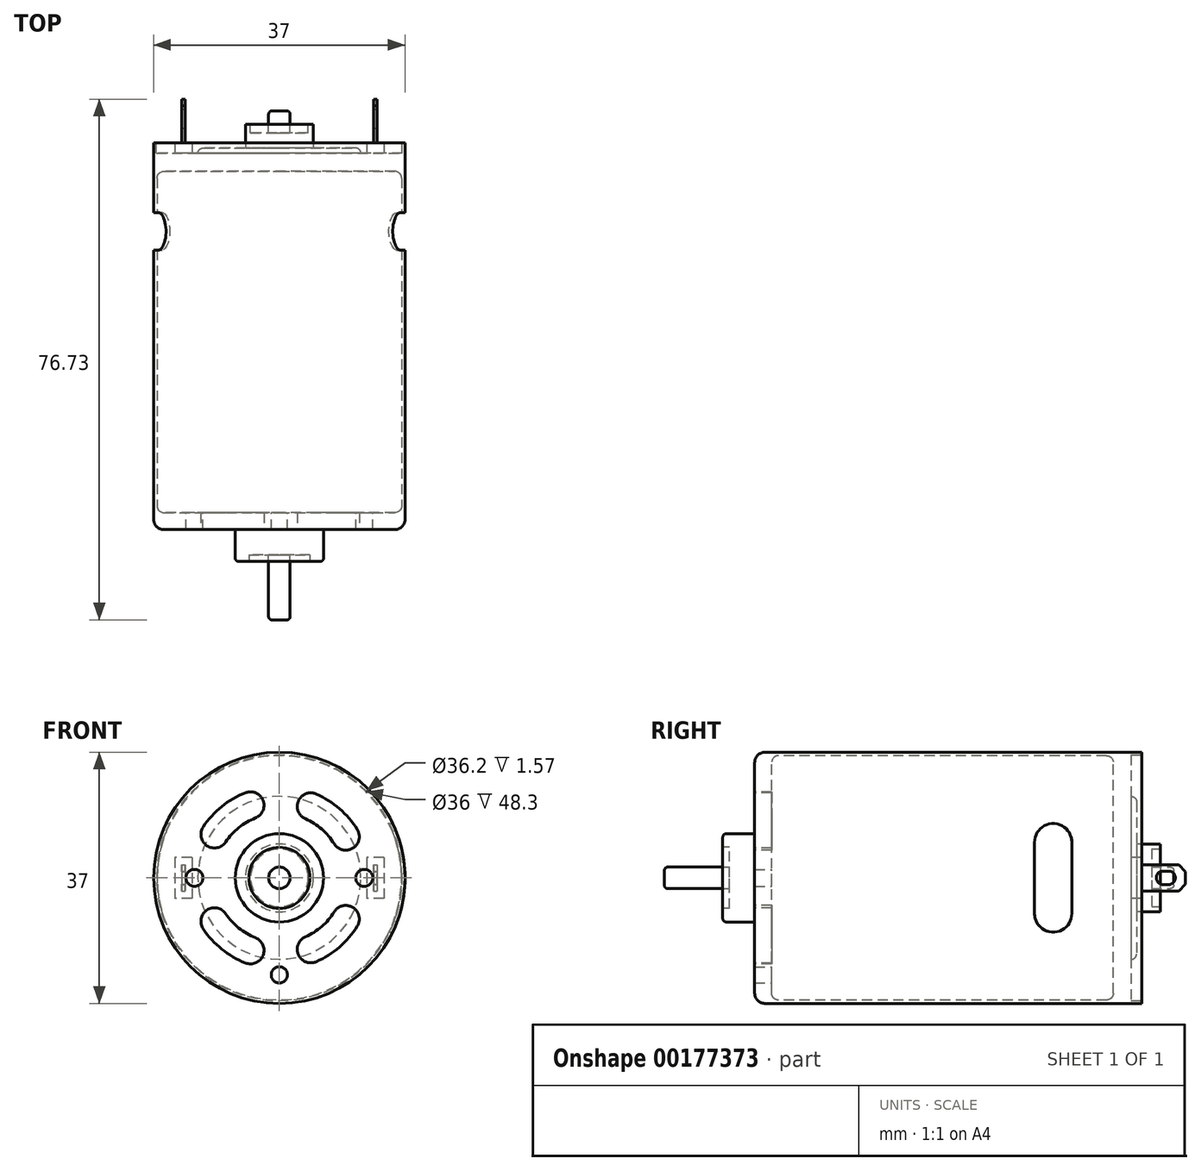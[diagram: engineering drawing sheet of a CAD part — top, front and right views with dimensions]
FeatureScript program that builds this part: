
annotation { "Feature Type Name" : "Feature", "Feature Type Description" : "" }
export const myFeature = defineFeature(function(context is Context, id is Id, definition is map)
    precondition{}
    {
        {
            var Q0;
            Q0=qCreatedBy(makeId("Front.planeOp"),FACE);
            var sketch = newSketch(context, id + "F0", { "sketchPlane" : qUnion([Q0])});
            skCircle(sketch, "E0", {"center": v(0, 0) * mm, "radius": 18.5 * mm});
            skSolve(sketch);
        }
        {
            var Q0;
            Q0 = qSketchRegion(id + "F0", true);
            extrude(context, id + "F1", {"entities" : qUnion([Q0]), "depth" : 57 * mm, "offsetDistance" : 25 * mm});
        }
        {
            var Q0;
            Q0=makeQuery(id+"F1.opExtrude","CAP_FACE",FACE,{"disambiguationData":[OSD([sQuery(id+"F0.wireOp",EDGE,"E0")])],"isStart":false});
            var sketch = newSketch(context, id + "F2", { "sketchPlane" : qUnion([Q0])});
            skCircle(sketch, "E1", {"center": v(0, 0) * mm, "radius": 6.5 * mm});
            skSolve(sketch);
        }
        {
            var Q0;
            Q0 = qSketchRegion(id + "F2", true);
            extrude(context, id + "F3", {"entities" : qUnion([Q0]), "operationType" : NewBodyOperationType.ADD, "depth" : 4.7 * mm, "offsetDistance" : 25 * mm});
        }
        {
            var Q0;
            Q0=makeQuery(id+"F3.opExtrude","CAP_FACE",FACE,{"disambiguationData":[OSD([sQuery(id+"F2.wireOp",EDGE,"E1")])],"isStart":false});
            var sketch = newSketch(context, id + "F4", { "sketchPlane" : qUnion([Q0])});
            skCircle(sketch, "E2", {"center": v(0, 0) * mm, "radius": 4.5 * mm});
            skSolve(sketch);
        }
        {
            var Q0;
            Q0 = qSketchRegion(id + "F4", true);
            extrude(context, id + "F5", {"entities" : qUnion([Q0]), "operationType" : NewBodyOperationType.REMOVE, "oppositeDirection" : true, "depth" : 1 * mm, "offsetDistance" : 25 * mm});
        }
        {
            var Q0;
            Q0=makeQuery(id+"F5.boolean.opBoolean","COPY",FACE,{"derivedFrom":makeQuery(id+"F5.opExtrude","CAP_FACE",FACE,{"disambiguationData":[OSD([sQuery(id+"F4.wireOp",EDGE,"E2")])],"isStart":false})});
            var sketch = newSketch(context, id + "F6", { "sketchPlane" : qUnion([Q0])});
            skCircle(sketch, "E3", {"center": v(0, 0) * mm, "radius": 1.58 * mm});
            skSolve(sketch);
        }
        {
            var Q0;
            Q0 = qSketchRegion(id + "F6", true);
            extrude(context, id + "F7", {"entities" : qUnion([Q0]), "depth" : 9.6 * mm, "offsetDistance" : 25 * mm});
        }
        {
            var Q0;
            Q0=makeQuery(id+"F3.opExtrude","CAP_EDGE",EDGE,{"disambiguationData":[OSD([sQuery(id+"F2.wireOp",EDGE,"E1")])],"isStart":false});
            fillet(context, id + "F8", {"entities" : qUnion([Q0]), "radius" : 0.5 * mm, "tangentPropagation" : true, "allowEdgeOverflow" : false});
        }
        {
            var Q0;
            Q0=makeQuery(id+"F1.opExtrude","CAP_EDGE",EDGE,{"disambiguationData":[OSD([sQuery(id+"F0.wireOp",EDGE,"E0")])],"isStart":false});
            fillet(context, id + "F9", {"entities" : qUnion([Q0]), "radius" : 1.5 * mm, "tangentPropagation" : true, "allowEdgeOverflow" : false});
        }
        {
            var Q0;
            Q0=makeQuery(id+"F1.opExtrude","CAP_FACE",FACE,{"disambiguationData":[OSD([sQuery(id+"F0.wireOp",EDGE,"E0")])],"isStart":true});
            var sketch = newSketch(context, id + "F10", { "sketchPlane" : qUnion([Q0])});
            skCircle(sketch, "E4", {"center": v(0, 0) * mm, "radius": 18.1 * mm});
            skSolve(sketch);
        }
        {
            var Q0;
            Q0 = qSketchRegion(id + "F10", true);
            extrude(context, id + "F11", {"entities" : qUnion([Q0]), "operationType" : NewBodyOperationType.REMOVE, "oppositeDirection" : true, "depth" : 1.57 * mm, "offsetDistance" : 25 * mm});
        }
        {
            var Q0;
            Q0=makeQuery(id+"F11.boolean.opBoolean","COPY",FACE,{"derivedFrom":makeQuery(id+"F11.opExtrude","CAP_FACE",FACE,{"disambiguationData":[OSD([sQuery(id+"F10.wireOp",EDGE,"E4")])],"isStart":false})});
            var sketch = newSketch(context, id + "F12", { "sketchPlane" : qUnion([Q0])});
            skLineSegment(sketch, "E5.bottom", {"start": v(-15.4, 3) * mm, "end": v(-12.85, 3) * mm});
            skLineSegment(sketch, "E5.top", {"start": v(-15.4, -3) * mm, "end": v(-12.85, -3) * mm});
            skLineSegment(sketch, "E5.left", {"start": v(-15.4, 3) * mm, "end": v(-15.4, -3) * mm});
            skLineSegment(sketch, "E5.right", {"start": v(-12.85, 3) * mm, "end": v(-12.85, -3) * mm});
            skLineSegment(sketch, "E6.bottom", {"start": v(12.85, 3) * mm, "end": v(15.4, 3) * mm});
            skLineSegment(sketch, "E6.top", {"start": v(12.85, -3) * mm, "end": v(15.4, -3) * mm});
            skLineSegment(sketch, "E6.left", {"start": v(12.85, 3) * mm, "end": v(12.85, -3) * mm});
            skLineSegment(sketch, "E6.right", {"start": v(15.4, 3) * mm, "end": v(15.4, -3) * mm});
            skSolve(sketch);
        }
        {
            var Q0;
            Q0 = qSketchRegion(id + "F12", true);
            extrude(context, id + "F13", {"entities" : qUnion([Q0]), "depth" : 1.5 * mm, "offsetDistance" : 25 * mm});
        }
        {
            var Q0;
            Q0=makeQuery(id+"F13.opExtrude","CAP_FACE",FACE,{"disambiguationData":[OSD([sQuery(id+"F12.wireOp",EDGE,"E6.bottom"),sQuery(id+"F12.wireOp",EDGE,"E6.top"),sQuery(id+"F12.wireOp",EDGE,"E6.left"),sQuery(id+"F12.wireOp",EDGE,"E6.right")])],"isStart":false});
            var sketch = newSketch(context, id + "F14", { "sketchPlane" : qUnion([Q0])});
            skLineSegment(sketch, "E7.bottom", {"start": v(14.38, 1.94) * mm, "end": v(13.88, 1.94) * mm});
            skLineSegment(sketch, "E7.top", {"start": v(14.38, -1.93) * mm, "end": v(13.88, -1.93) * mm});
            skLineSegment(sketch, "E7.left", {"start": v(14.38, 1.93) * mm, "end": v(14.38, -1.93) * mm});
            skLineSegment(sketch, "E7.right", {"start": v(13.88, 1.93) * mm, "end": v(13.88, -1.93) * mm});
            skLineSegment(sketch, "E8", {"start": v(14.12, 3) * mm, "end": v(14.12, -3) * mm, "construction": true});
            skLineSegment(sketch, "E9", {"start": v(15.4, 0) * mm, "end": v(12.85, 0) * mm, "construction": true});
            skLineSegment(sketch, "E10.MirrorCS", {"start": v(-14.38, 1.94) * mm, "end": v(-13.88, 1.94) * mm});
            skLineSegment(sketch, "E11.MirrorCS", {"start": v(-14.38, -1.93) * mm, "end": v(-13.88, -1.93) * mm});
            skLineSegment(sketch, "E12.MirrorCS", {"start": v(-13.88, 1.93) * mm, "end": v(-13.88, -1.93) * mm});
            skLineSegment(sketch, "E13.MirrorCS", {"start": v(-14.38, 1.93) * mm, "end": v(-14.38, -1.93) * mm});
            skSolve(sketch);
        }
        {
            var Q0;
            Q0 = qSketchRegion(id + "F14", true);
            extrude(context, id + "F15", {"entities" : qUnion([Q0]), "depth" : 6.5 * mm, "offsetDistance" : 25 * mm});
        }
        {
            var Q0;
            Q0=makeQuery(id+"F15.opExtrude","SWEPT_FACE",FACE,{"disambiguationData":[OSD([sQuery(id+"F14.wireOp",EDGE,"E13.MirrorCS")])]});
            var sketch = newSketch(context, id + "F16", { "sketchPlane" : qUnion([Q0])});
            skLineSegment(sketch, "E14", {"start": v(5.43, 1.94) * mm, "end": v(6.43, 0.94) * mm});
            skLineSegment(sketch, "E15", {"start": v(6.43, 0.94) * mm, "end": v(6.43, -0.93) * mm});
            skLineSegment(sketch, "E16", {"start": v(6.43, -0.93) * mm, "end": v(5.43, -1.93) * mm});
            skLineSegment(sketch, "E17", {"start": v(5.43, -1.93) * mm, "end": v(5.43, -3.02) * mm});
            skLineSegment(sketch, "E18", {"start": v(5.43, -3.02) * mm, "end": v(9.56, -3.02) * mm});
            skLineSegment(sketch, "E19", {"start": v(9.56, -3.02) * mm, "end": v(9.56, 2.65) * mm});
            skLineSegment(sketch, "E20", {"start": v(9.56, 2.65) * mm, "end": v(5.36, 2.65) * mm});
            skLineSegment(sketch, "E21", {"start": v(5.36, 2.65) * mm, "end": v(5.43, 1.94) * mm});
            skArc(sketch, "E22", {"start": v(3.93, -1) * mm, "mid": v(4.93, 0) * mm, "end": v(3.93, 1) * mm});
            skArc(sketch, "E23", {"start": v(3.13, 1) * mm, "mid": v(2.13, 0) * mm, "end": v(3.13, -1) * mm});
            skLineSegment(sketch, "E24", {"start": v(3.13, 1) * mm, "end": v(3.93, 1) * mm});
            skLineSegment(sketch, "E25", {"start": v(3.93, -1) * mm, "end": v(3.13, -1) * mm});
            skSolve(sketch);
        }
        {
            var Q0;
            Q0=makeQuery(id+"F16.imprint","IMPRINT",FACE,{"disambiguationData":[TD([[makeQuery(id+"F16.imprint","IMPRINT",EDGE,{"derivedFrom":sQuery(id+"F16.wireOp",EDGE,"E22")}),1.0]])]});
            var Q1;
            {var subQ0=sQuery(id+"F16.wireOp",EDGE,"E14");Q1=makeQuery(id+"F16.imprint","IMPRINT",FACE,{"disambiguationData":[TD([[makeQuery(id+"F16.imprint","IMPRINT",EDGE,{"derivedFrom":subQ0}),1.0]])]});}
            var Q2;
            {var subQ0=sQuery(id+"F16.wireOp",EDGE,"E16");Q2=makeQuery(id+"F16.imprint","IMPRINT",FACE,{"disambiguationData":[TD([[makeQuery(id+"F16.imprint","IMPRINT",EDGE,{"derivedFrom":subQ0}),1.0]])]});}
            var Q3;
            {var subQ10=sQuery(id+"F16.wireOp",EDGE,"E15");Q3=makeQuery(id+"F16.imprint","IMPRINT",FACE,{"disambiguationData":[TD([[makeQuery(id+"F16.imprint","IMPRINT",EDGE,{"derivedFrom":subQ10}),1.0]])]});}
            extrude(context, id + "F17", {"entities" : qUnion([Q0, Q1, Q2, Q3]), "operationType" : NewBodyOperationType.REMOVE, "endBound" : BoundingType.THROUGH_ALL, "oppositeDirection" : true, "depth" : 25 * mm, "offsetDistance" : 25 * mm});
        }
        {
            var Q0;
            Q0=makeQuery(id+"F11.boolean.opBoolean","COPY",FACE,{"derivedFrom":makeQuery(id+"F11.opExtrude","CAP_FACE",FACE,{"disambiguationData":[OSD([sQuery(id+"F10.wireOp",EDGE,"E4")])],"isStart":false})});
            var sketch = newSketch(context, id + "F18", { "sketchPlane" : qUnion([Q0])});
            skCircle(sketch, "E26", {"center": v(0, 0) * mm, "radius": 12 * mm});
            skSolve(sketch);
        }
        {
            var Q0;
            Q0 = qSketchRegion(id + "F18", true);
            extrude(context, id + "F19", {"entities" : qUnion([Q0]), "operationType" : NewBodyOperationType.ADD, "depth" : 0.8 * mm, "offsetDistance" : 25 * mm});
        }
        {
            var Q0;
            Q0=makeQuery(id+"F19.opExtrude","CAP_FACE",FACE,{"disambiguationData":[OSD([sQuery(id+"F18.wireOp",EDGE,"E26")])],"isStart":false});
            var sketch = newSketch(context, id + "F20", { "sketchPlane" : qUnion([Q0])});
            skCircle(sketch, "E27", {"center": v(0, 0) * mm, "radius": 5 * mm});
            skSolve(sketch);
        }
        {
            var Q0;
            Q0 = qSketchRegion(id + "F20", true);
            extrude(context, id + "F21", {"entities" : qUnion([Q0]), "operationType" : NewBodyOperationType.ADD, "depth" : 3.5 * mm, "offsetDistance" : 25 * mm});
        }
        {
            var Q0;
            Q0=makeQuery(id+"F21.opExtrude","CAP_FACE",FACE,{"disambiguationData":[OSD([sQuery(id+"F20.wireOp",EDGE,"E27")])],"isStart":false});
            var sketch = newSketch(context, id + "F22", { "sketchPlane" : qUnion([Q0])});
            skCircle(sketch, "E28", {"center": v(0, 0) * mm, "radius": 4.25 * mm});
            skSolve(sketch);
        }
        {
            var Q0;
            Q0 = qSketchRegion(id + "F22", true);
            extrude(context, id + "F23", {"entities" : qUnion([Q0]), "operationType" : NewBodyOperationType.REMOVE, "oppositeDirection" : true, "depth" : 1.3 * mm, "offsetDistance" : 25 * mm});
        }
        {
            var Q0;
            Q0=makeQuery(id+"F7.opExtrude","CAP_FACE",FACE,{"disambiguationData":[OSD([sQuery(id+"F6.wireOp",EDGE,"E3")])],"isStart":false});
            extrude(context, id + "F24", {"entities" : qUnion([Q0]), "operationType" : NewBodyOperationType.ADD, "oppositeDirection" : true, "depth" : 75 * mm, "offsetDistance" : 25 * mm});
        }
        {
            var Q0;
            Q0=makeQuery(id+"F19.opExtrude","CAP_EDGE",EDGE,{"disambiguationData":[OSD([sQuery(id+"F18.wireOp",EDGE,"E26")])],"isStart":false});
            fillet(context, id + "F25", {"entities" : qUnion([Q0]), "radius" : 0.8 * mm, "tangentPropagation" : true, "allowEdgeOverflow" : false});
        }
        {
            var Q0;
            Q0=makeQuery(id+"F24.opExtrude","CAP_EDGE",EDGE,{"disambiguationData":[OSD([sQuery(id+"F6.wireOp",EDGE,"E3")])],"isStart":false});
            var Q1;
            Q1=makeQuery(id+"F7.opExtrude","CAP_EDGE",EDGE,{"disambiguationData":[OSD([sQuery(id+"F6.wireOp",EDGE,"E3")])],"isStart":false});
            fillet(context, id + "F26", {"entities" : qUnion([Q0, Q1]), "radius" : 0.5 * mm, "tangentPropagation" : true, "allowEdgeOverflow" : false});
        }
        {
            var Q0;
            Q0=makeQuery(id+"F1.opExtrude","CAP_FACE",FACE,{"disambiguationData":[OSD([sQuery(id+"F0.wireOp",EDGE,"E0")])],"isStart":false});
            var sketch = newSketch(context, id + "F27", { "sketchPlane" : qUnion([Q0])});
            skPoint(sketch, "E29", {"position": v(-12.5, 0) * mm});
            skPoint(sketch, "E30", {"position": v(12.5, 0) * mm});
            skSolve(sketch);
        }
        {
            var Q0;
            Q0=sQuery(id+"F27.wireOp",VERTEX,"E29");
            var Q1;
            Q1=sQuery(id+"F27.wireOp",VERTEX,"E30");
            var Q2;
            Q2=makeQuery(id+"F1.opExtrude","SWEPT_BODY",BODY,{"disambiguationData":[OSD([sQuery(id+"F0.wireOp",EDGE,"E0")])]});
            hole(context, id + "F28", {"style" : HoleStyle.SIMPLE, "endStyle" : HoleEndStyle.BLIND, "standardTappedOrClearance" : lookupTablePath({ "standard" : "ISO", "engagement" : "75%", "pitch" : "0.5 mm", "size" : "M3", "type" : "Tapped" }), "standardBlindInLast" : lookupTablePath({ "standard" : "ISO", "engagement" : "75%", "pitch" : "0.5 mm", "size" : "M3", "type" : "Tapped" }), "holeDiameter" : 2.5 * mm, "majorDiameter" : 3 * mm, "showTappedDepth" : true, "holeDepth" : 10 * mm, "tappedDepth" : 8.5 * mm, "tapClearance" : 3, "locations" : qUnion([Q0, Q1]), "scope" : qUnion([Q2]), "startStyle" : HoleStartStyle.PART});
        }
        {
            var Q0;
            Q0=makeQuery(id+"F1.opExtrude","CAP_FACE",FACE,{"disambiguationData":[OSD([sQuery(id+"F0.wireOp",EDGE,"E0")])],"isStart":false});
            var sketch = newSketch(context, id + "F29", { "sketchPlane" : qUnion([Q0])});
            skPoint(sketch, "E31", {"position": v(0, -14.3) * mm});
            skSolve(sketch);
        }
        {
            var Q0;
            Q0=sQuery(id+"F29.wireOp",VERTEX,"E31");
            var Q1;
            Q1=makeQuery(id+"F1.opExtrude","SWEPT_BODY",BODY,{"disambiguationData":[OSD([sQuery(id+"F0.wireOp",EDGE,"E0")])]});
            hole(context, id + "F30", {"style" : HoleStyle.SIMPLE, "endStyle" : HoleEndStyle.BLIND, "standardTappedOrClearance" : lookupTablePath({ "standard" : "ISO", "size" : "2.4", "type" : "Drilled" }), "standardBlindInLast" : lookupTablePath({ "standard" : "ISO", "size" : "2.4", "type" : "Drilled" }), "holeDiameter" : 2.4 * mm, "majorDiameter" : 3 * mm, "holeDepth" : 5 * mm, "tappedDepth" : 8.5 * mm, "tapClearance" : 3, "locations" : qUnion([Q0]), "scope" : qUnion([Q1]), "startStyle" : HoleStartStyle.PART});
        }
        {
            var Q0;
            Q0=makeQuery(id+"F1.opExtrude","CAP_FACE",FACE,{"disambiguationData":[OSD([sQuery(id+"F0.wireOp",EDGE,"E0")])],"isStart":false});
            var sketch = newSketch(context, id + "F31", { "sketchPlane" : qUnion([Q0])});
            skCircle(sketch, "E32", {"center": v(0, 0) * mm, "radius": 9.5 * mm, "construction": true});
            skCircle(sketch, "E33", {"center": v(0, 0) * mm, "radius": 13.5 * mm, "construction": true});
            skCircle(sketch, "E34", {"center": v(0, 0) * mm, "radius": 11.5 * mm, "construction": true});
            skArc(sketch, "E35", {"start": v(-3.52, 8.82) * mm, "mid": v(-2.4, 11.42) * mm, "end": v(-5, 12.54) * mm});
            skArc(sketch, "E36", {"start": v(5.44, 12.36) * mm, "mid": v(2.8, 11.33) * mm, "end": v(3.83, 8.7) * mm});
            skArc(sketch, "E37", {"start": v(8.07, 5.01) * mm, "mid": v(10.82, 4.37) * mm, "end": v(11.47, 7.12) * mm});
            skArc(sketch, "E38", {"start": v(11.47, -7.12) * mm, "mid": v(10.82, -4.37) * mm, "end": v(8.07, -5.01) * mm});
            skArc(sketch, "E39", {"start": v(-5, -12.54) * mm, "mid": v(-2.4, -11.42) * mm, "end": v(-3.52, -8.82) * mm});
            skArc(sketch, "E40", {"start": v(-7.9, -5.3) * mm, "mid": v(-10.67, -4.74) * mm, "end": v(-11.21, -7.52) * mm});
            skArc(sketch, "E41", {"start": v(-11.21, 7.52) * mm, "mid": v(-10.67, 4.74) * mm, "end": v(-7.9, 5.3) * mm});
            skArc(sketch, "E42", {"start": v(-3.52, 8.82) * mm, "mid": v(-5.97, 7.39) * mm, "end": v(-7.9, 5.3) * mm});
            skArc(sketch, "E43", {"start": v(-5, 12.54) * mm, "mid": v(-8.49, 10.5) * mm, "end": v(-11.21, 7.52) * mm});
            skArc(sketch, "E44", {"start": v(8.07, 5.01) * mm, "mid": v(6.23, 7.17) * mm, "end": v(3.83, 8.7) * mm});
            skArc(sketch, "E45", {"start": v(11.47, 7.12) * mm, "mid": v(8.85, 10.2) * mm, "end": v(5.44, 12.36) * mm});
            skArc(sketch, "E46", {"start": v(-11.21, -7.52) * mm, "mid": v(-8.49, -10.5) * mm, "end": v(-5, -12.54) * mm});
            skArc(sketch, "E47", {"start": v(-7.9, -5.3) * mm, "mid": v(-5.97, -7.39) * mm, "end": v(-3.52, -8.82) * mm});
            skArc(sketch, "E48", {"start": v(3.83, -8.7) * mm, "mid": v(2.8, -11.33) * mm, "end": v(5.44, -12.36) * mm});
            skArc(sketch, "E49", {"start": v(3.83, -8.7) * mm, "mid": v(6.23, -7.17) * mm, "end": v(8.07, -5.01) * mm});
            skPoint(sketch, "E50.endSnap0", {"position": v(6.23, -7.17) * mm});
            skArc(sketch, "E51", {"start": v(5.44, -12.36) * mm, "mid": v(8.85, -10.2) * mm, "end": v(11.47, -7.12) * mm});
            skSolve(sketch);
        }
        {
            var Q0;
            Q0 = qSketchRegion(id + "F31", true);
            extrude(context, id + "F32", {"entities" : qUnion([Q0]), "operationType" : NewBodyOperationType.REMOVE, "oppositeDirection" : true, "depth" : 2.5 * mm, "offsetDistance" : 25 * mm});
        }
        {
            var Q0;
            Q0=qCreatedBy(makeId("Right.planeOp"),FACE);
            cPlane(context, id + "F33", {"entities" : qUnion([Q0]), "cplaneType" : CPlaneType.OFFSET, "offset" : 18.5 * mm, "width" : 150 * mm, "height" : 150 * mm});
        }
        {
            var Q0;
            Q0=qCreatedBy(id+"F33.planeOp",FACE);
            var sketch = newSketch(context, id + "F34", { "sketchPlane" : qUnion([Q0])});
            skArc(sketch, "E52", {"start": v(-10.3, 5.25) * mm, "mid": v(-13.05, 8) * mm, "end": v(-15.8, 5.25) * mm});
            skArc(sketch, "E53", {"start": v(-15.8, -5.25) * mm, "mid": v(-13.05, -8) * mm, "end": v(-10.3, -5.25) * mm});
            skLineSegment(sketch, "E54", {"start": v(-15.8, 5.25) * mm, "end": v(-15.8, -5.25) * mm});
            skLineSegment(sketch, "E55", {"start": v(-10.3, -5.25) * mm, "end": v(-10.3, 5.25) * mm});
            skSolve(sketch);
        }
        {
            var Q0;
            Q0 = qSketchRegion(id + "F34", true);
            extrude(context, id + "F35", {"entities" : qUnion([Q0]), "operationType" : NewBodyOperationType.REMOVE, "endBound" : BoundingType.THROUGH_ALL, "oppositeDirection" : true, "depth" : 25 * mm, "offsetDistance" : 25 * mm});
        }
        {
            var Q0;
            Q0=makeQuery(id+"F32.boolean.opBoolean","COPY",FACE,{"derivedFrom":makeQuery(id+"F32.opExtrude","CAP_FACE",FACE,{"disambiguationData":[OSD([sQuery(id+"F31.wireOp",EDGE,"E36"),sQuery(id+"F31.wireOp",EDGE,"E37"),sQuery(id+"F31.wireOp",EDGE,"E44"),sQuery(id+"F31.wireOp",EDGE,"E45")])],"isStart":false})});
            var sketch = newSketch(context, id + "F36", { "sketchPlane" : qUnion([Q0])});
            skCircle(sketch, "E56", {"center": v(0, 0) * mm, "radius": 18 * mm});
            skSolve(sketch);
        }
        {
            var Q0;
            Q0 = qSketchRegion(id + "F36", true);
            extrude(context, id + "F37", {"entities" : qUnion([Q0]), "operationType" : NewBodyOperationType.REMOVE, "oppositeDirection" : true, "depth" : 50.3 * mm, "offsetDistance" : 25 * mm});
        }
        {
            var Q0;
            Q0=makeQuery(id+"F37.boolean.opBoolean","COPY",EDGE,{"derivedFrom":makeQuery(id+"F37.opExtrude","CAP_EDGE",EDGE,{"disambiguationData":[OSD([sQuery(id+"F36.wireOp",EDGE,"E56")])],"isStart":false})});
            var Q1;
            Q1=makeQuery(id+"F37.boolean.opBoolean","COPY",EDGE,{"derivedFrom":makeQuery(id+"F37.opExtrude","CAP_EDGE",EDGE,{"disambiguationData":[OSD([sQuery(id+"F36.wireOp",EDGE,"E56")])],"isStart":true})});
            fillet(context, id + "F38", {"entities" : qUnion([Q0, Q1]), "radius" : 1 * mm, "tangentPropagation" : true, "allowEdgeOverflow" : false});
        }
    });
